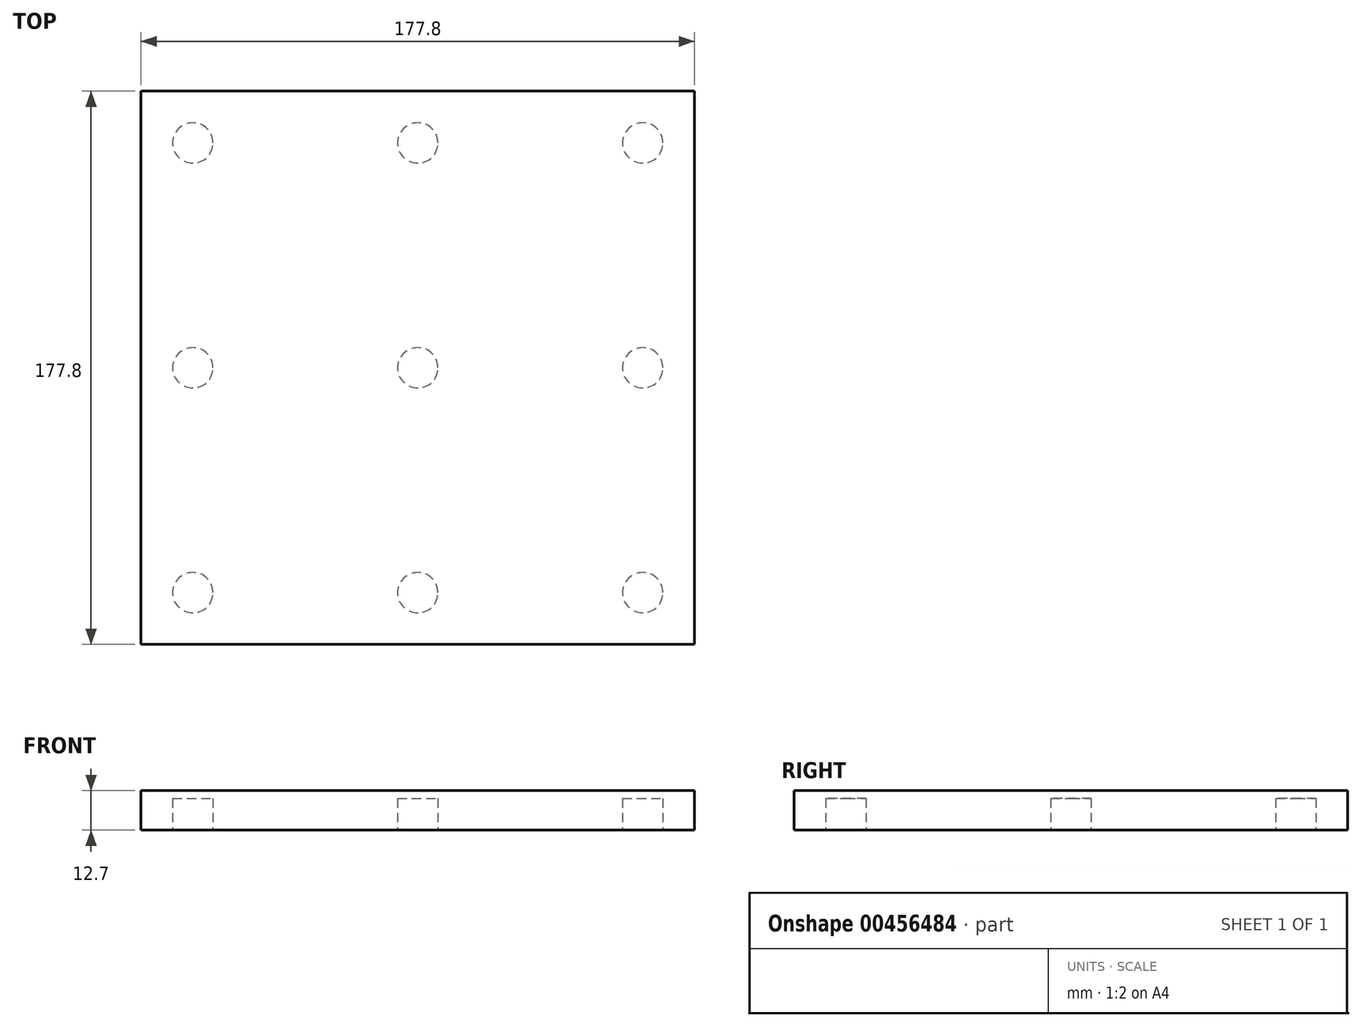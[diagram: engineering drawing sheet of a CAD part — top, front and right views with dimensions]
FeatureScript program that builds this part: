
annotation { "Feature Type Name" : "Feature", "Feature Type Description" : "" }
export const myFeature = defineFeature(function(context is Context, id is Id, definition is map)
    precondition{}
    {
        {
            var Q0;
            Q0=qCreatedBy(makeId("Top.planeOp"),FACE);
            var sketch = newSketch(context, id + "F0", { "sketchPlane" : qUnion([Q0])});
            skLineSegment(sketch, "E0.bottom", {"start": v(-88.9, -88.9) * mm, "end": v(88.9, -88.9) * mm});
            skLineSegment(sketch, "E0.top", {"start": v(-88.9, 88.9) * mm, "end": v(88.9, 88.9) * mm});
            skLineSegment(sketch, "E0.left", {"start": v(-88.9, -88.9) * mm, "end": v(-88.9, 88.9) * mm});
            skLineSegment(sketch, "E0.right", {"start": v(88.9, -88.9) * mm, "end": v(88.9, 88.9) * mm});
            skPoint(sketch, "E0.middle", {"position": v(0, 0) * mm});
            skSolve(sketch);
        }
        {
            var Q0;
            Q0=makeQuery(id+"F0.imprint","IMPRINT",FACE,{"disambiguationData":[TD([[makeQuery(id+"F0.imprint","IMPRINT",EDGE,{"derivedFrom":sQuery(id+"F0.wireOp",EDGE,"E0.bottom")}),1.0]])]});
            extrude(context, id + "F1", {"entities" : qUnion([Q0]), "depth" : 12.7 * mm, "offsetDistance" : 25.4 * mm});
        }
        {
            var Q0;
            Q0=makeQuery(id+"F1.opExtrude","CAP_FACE",FACE,{"disambiguationData":[OSD([sQuery(id+"F0.wireOp",EDGE,"E0.bottom"),sQuery(id+"F0.wireOp",EDGE,"E0.top"),sQuery(id+"F0.wireOp",EDGE,"E0.left"),sQuery(id+"F0.wireOp",EDGE,"E0.right")])],"isStart":true});
            var sketch = newSketch(context, id + "F2", { "sketchPlane" : qUnion([Q0])});
            skCircle(sketch, "E1", {"center": v(-72.26, 72.26) * mm, "radius": 6.48 * mm});
            skCircle(sketch, "E2", {"center": v(-72.26, -72.26) * mm, "radius": 6.48 * mm});
            skCircle(sketch, "E3", {"center": v(72.26, -72.26) * mm, "radius": 6.48 * mm});
            skCircle(sketch, "E4", {"center": v(72.26, 72.26) * mm, "radius": 6.48 * mm});
            skCircle(sketch, "E5", {"center": v(0, 72.26) * mm, "radius": 6.48 * mm});
            skCircle(sketch, "E6", {"center": v(72.26, 0) * mm, "radius": 6.48 * mm});
            skCircle(sketch, "E7", {"center": v(0, -72.26) * mm, "radius": 6.48 * mm});
            skCircle(sketch, "E8", {"center": v(-72.26, 0) * mm, "radius": 6.48 * mm});
            skCircle(sketch, "E9", {"center": v(0, 0) * mm, "radius": 6.48 * mm});
            skSolve(sketch);
        }
        {
            var Q0;
            Q0=makeQuery(id+"F2.imprint","IMPRINT",FACE,{"disambiguationData":[TD([[makeQuery(id+"F2.imprint","IMPRINT",EDGE,{"derivedFrom":sQuery(id+"F2.wireOp",EDGE,"E4")}),1.0]])]});
            var Q1;
            Q1=makeQuery(id+"F2.imprint","IMPRINT",FACE,{"disambiguationData":[TD([[makeQuery(id+"F2.imprint","IMPRINT",EDGE,{"derivedFrom":sQuery(id+"F2.wireOp",EDGE,"E3")}),1.0]])]});
            var Q2;
            Q2=makeQuery(id+"F2.imprint","IMPRINT",FACE,{"disambiguationData":[TD([[makeQuery(id+"F2.imprint","IMPRINT",EDGE,{"derivedFrom":sQuery(id+"F2.wireOp",EDGE,"E7")}),1.0]])]});
            var Q3;
            Q3=makeQuery(id+"F2.imprint","IMPRINT",FACE,{"disambiguationData":[TD([[makeQuery(id+"F2.imprint","IMPRINT",EDGE,{"derivedFrom":sQuery(id+"F2.wireOp",EDGE,"E2")}),1.0]])]});
            var Q4;
            Q4=makeQuery(id+"F2.imprint","IMPRINT",FACE,{"disambiguationData":[TD([[makeQuery(id+"F2.imprint","IMPRINT",EDGE,{"derivedFrom":sQuery(id+"F2.wireOp",EDGE,"E8")}),1.0]])]});
            var Q5;
            Q5=makeQuery(id+"F2.imprint","IMPRINT",FACE,{"disambiguationData":[TD([[makeQuery(id+"F2.imprint","IMPRINT",EDGE,{"derivedFrom":sQuery(id+"F2.wireOp",EDGE,"E5")}),1.0]])]});
            var Q6;
            Q6=makeQuery(id+"F2.imprint","IMPRINT",FACE,{"disambiguationData":[TD([[makeQuery(id+"F2.imprint","IMPRINT",EDGE,{"derivedFrom":sQuery(id+"F2.wireOp",EDGE,"E1")}),1.0]])]});
            var Q7;
            Q7=makeQuery(id+"F2.imprint","IMPRINT",FACE,{"disambiguationData":[TD([[makeQuery(id+"F2.imprint","IMPRINT",EDGE,{"derivedFrom":sQuery(id+"F2.wireOp",EDGE,"E9")}),1.0]])]});
            var Q8;
            Q8=makeQuery(id+"F2.imprint","IMPRINT",FACE,{"disambiguationData":[TD([[makeQuery(id+"F2.imprint","IMPRINT",EDGE,{"derivedFrom":sQuery(id+"F2.wireOp",EDGE,"E6")}),1.0]])]});
            extrude(context, id + "F3", {"entities" : qUnion([Q0, Q1, Q2, Q3, Q4, Q5, Q6, Q7, Q8]), "operationType" : NewBodyOperationType.REMOVE, "oppositeDirection" : true, "depth" : 10.16 * mm, "offsetDistance" : 25.4 * mm});
        }
    });
